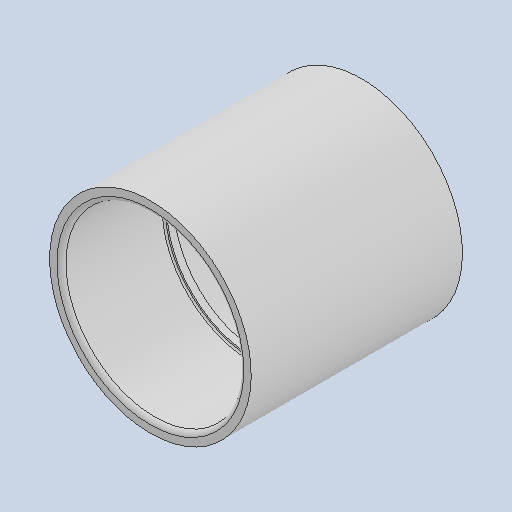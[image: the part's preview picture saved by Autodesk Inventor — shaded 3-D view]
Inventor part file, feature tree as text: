
AUTODESK INVENTOR PART (.ipt)
format: ipt  version: 2022 (Build 260153000, 153)  size: 151,040 bytes
history: native  units: in
note: dims shown in document units (in); Inventor stores cm internally (conversion verified against a paired STEP export)
features: fillet x1
ambient origin geometry x8: Origin, YZ Plane, XZ Plane, XY Plane, X Axis, Y Axis, Z Axis, Center Point
bodies: Solid1 (feature_tree)
feature tree (1):
  fillet  "Fillet2"  [1 undecoded]
note: 1 required parameter value undecoded (feature->parameter linkage not recoverable at this tier; creation-order binding heuristic only, values carry confidence <= 0.55)
